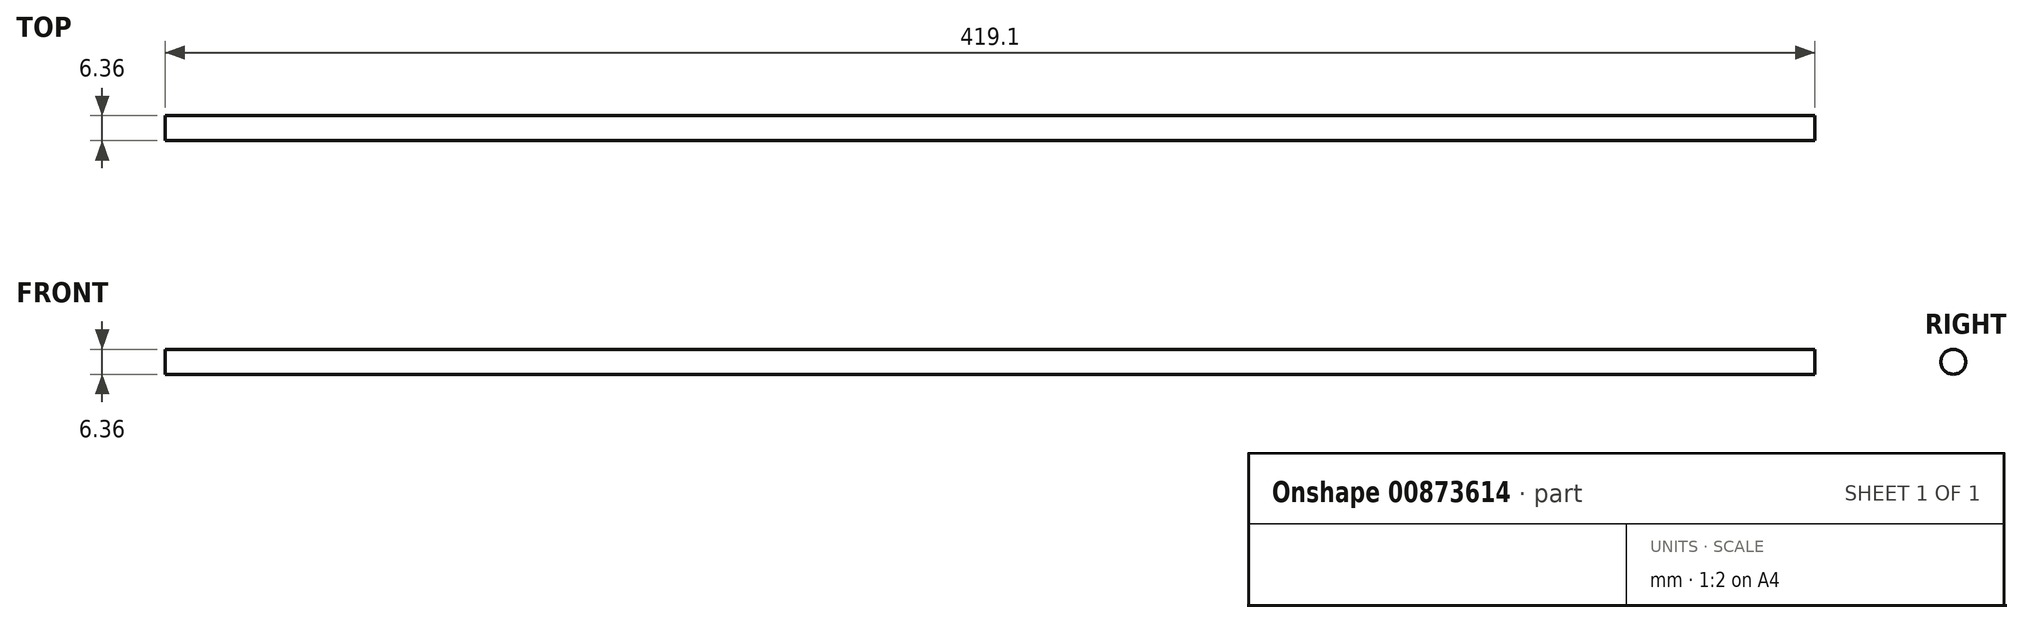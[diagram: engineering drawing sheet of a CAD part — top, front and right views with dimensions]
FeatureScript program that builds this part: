
annotation { "Feature Type Name" : "Feature", "Feature Type Description" : "" }
export const myFeature = defineFeature(function(context is Context, id is Id, definition is map)
    precondition{}
    {
        {
            var Q0;
            Q0=qCreatedBy(makeId("Right.planeOp"),FACE);
            var sketch = newSketch(context, id + "F0", { "sketchPlane" : qUnion([Q0])});
            skCircle(sketch, "E0", {"center": v(0, 0) * mm, "radius": 3.18 * mm});
            skSolve(sketch);
        }
        {
            var Q0;
            Q0 = qSketchRegion(id + "F0", true);
            extrude(context, id + "F1", {"entities" : qUnion([Q0]), "oppositeDirection" : true, "depth" : 419.1 * mm, "offsetDistance" : 25.4 * mm});
        }
    });
